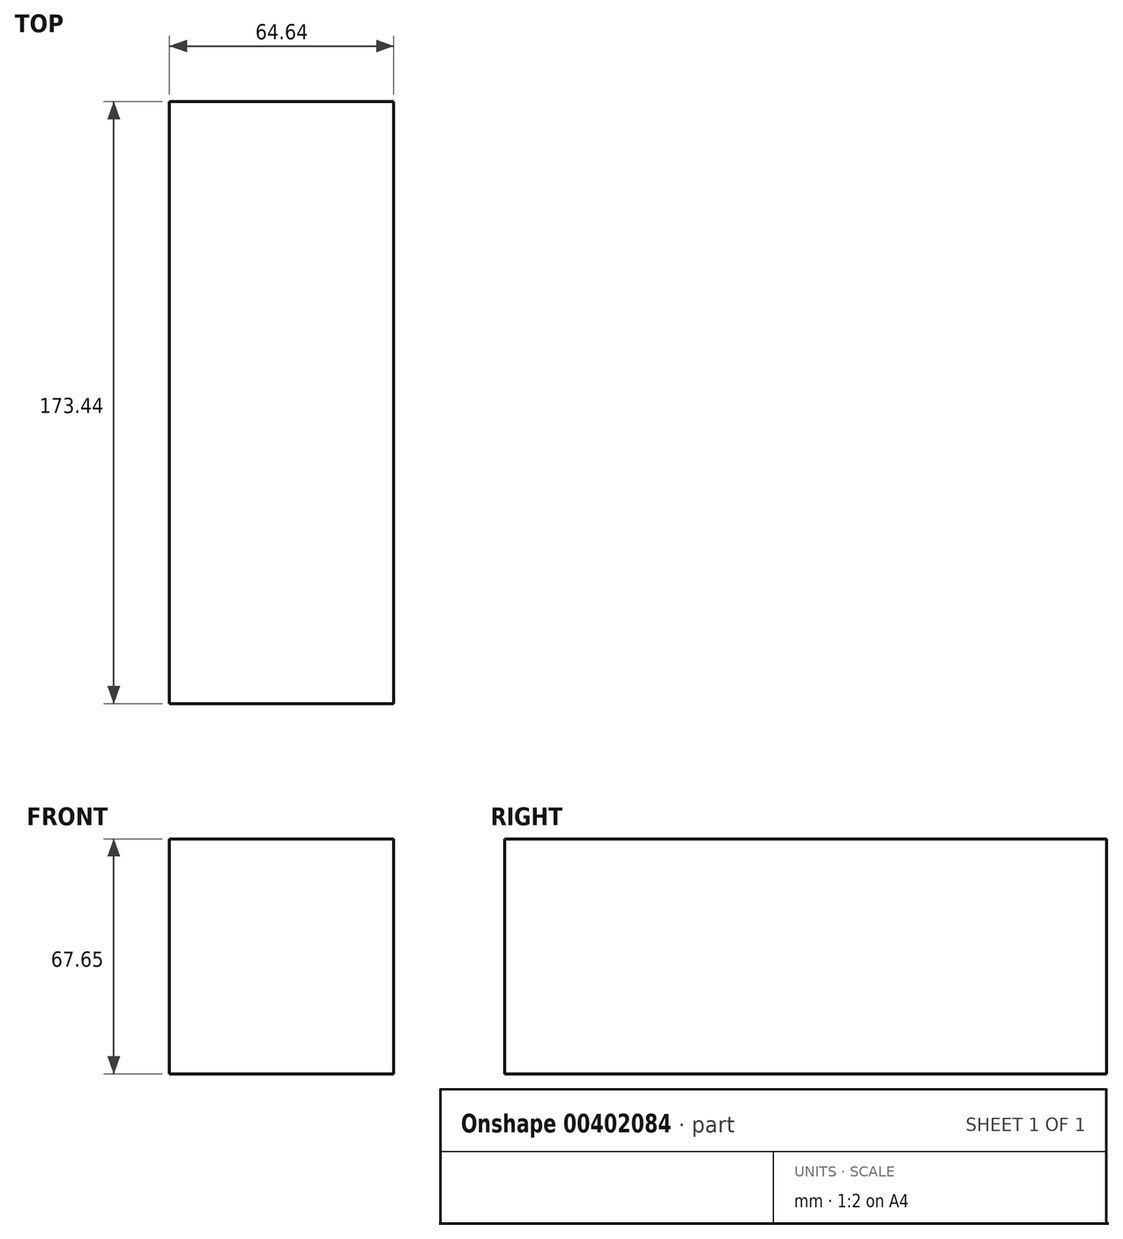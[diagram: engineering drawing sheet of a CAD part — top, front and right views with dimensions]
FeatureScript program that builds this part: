
annotation { "Feature Type Name" : "Feature", "Feature Type Description" : "" }
export const myFeature = defineFeature(function(context is Context, id is Id, definition is map)
    precondition{}
    {
        {
            var Q0;
            Q0=qCreatedBy(makeId("Front.planeOp"),FACE);
            var sketch = newSketch(context, id + "F0", { "sketchPlane" : qUnion([Q0])});
            skLineSegment(sketch, "E0.bottom", {"start": v(-26.4, -31.65) * mm, "end": v(38.24, -31.65) * mm});
            skLineSegment(sketch, "E0.top", {"start": v(-26.4, 36) * mm, "end": v(38.24, 36) * mm});
            skLineSegment(sketch, "E0.left", {"start": v(-26.4, -31.65) * mm, "end": v(-26.4, 36) * mm});
            skLineSegment(sketch, "E0.right", {"start": v(38.24, -31.65) * mm, "end": v(38.24, 36) * mm});
            skSolve(sketch);
        }
        {
            var Q0;
            Q0 = qSketchRegion(id + "F0", true);
            extrude(context, id + "F1", {"entities" : qUnion([Q0]), "depth" : 173.44 * mm});
        }
    });
